# Revit family: 635-00-001 DN100-150
name_source: partatom
category: Pipe Accessories
units: mm (PartAtom-declared; Revit-internal decimal feet)

## family parameters
Always vertical = No
Cut with Voids When Loaded = No
Part Type = Valve - Breaks Into
Round Connector Dimension = Use Diameter
Shared = No
Work Plane-Based = No

## types (3) — shared parameters
1 = 1 mm  [stored 0.00328084 ft]
10 = 10 mm  [stored 0.0328084 ft]
12 = 11 mm  [stored 0.0360892 ft]
2 = 2 mm  [stored 0.00656168 ft]
4 = 4 mm  [stored 0.0131234 ft]
DN100_PN16 = 635-133-00-166
DN125_ PN16 = 635-161-00-166
DN150_ PN16 = 635-188-00-166
Description_ = AVK SUPA MAXI™ TRANSITION COUPLING, PE100/PN16
Search_table = 635-00-001 DN100-150
URL product pages = https://www.avkvalves.com
zero-valued in all types: Default Elevation

## per-type parameters (varying)
- DN100_PN16: Bolt1=9 mm; Bolt2=10.35 mm  [stored 0.0339567 ft]; Bolt_End_dis=74 mm; Bore=50 mm  [stored 0.164042 ft]; Cap_Radius=30 mm  [stored 0.0984252 ft]; D=134 mm; D1=113.9 mm; D2=57.2 mm; D3=40.2 mm  [stored 0.13189 ft]; DN=100 mm; FL_T=61 mm  [stored 0.200131 ft]; FL_T2=30.5 mm  [stored 0.100066 ft]; FLange_T1=81.4 mm; L=547 mm; L1=281 mm; L3=164.1 mm; L4=180.51 mm; L4-L3=11.49 mm; L5=225.64 mm; OD=55 mm  [stored 0.180446 ft]; PCD=120.6 mm; Ring_Dia=72.5 mm  [stored 0.237861 ft]; Ring_Dia1=66.7 mm  [stored 0.218832 ft]; Ring_dia2=60.85 mm; Ring_dia3=66.94 mm; SR1=52 mm; SR2=66.5 mm  [stored 0.218176 ft]; Thickness=11 mm  [stored 0.0360892 ft]
- DN125_ PN16: Bolt1=8.7 mm  [stored 0.0285433 ft]; Bolt2=10.01 mm; Bolt_End_dis=75 mm; Bore=62.5 mm  [stored 0.205052 ft]; Cap_Radius=29 mm  [stored 0.0951444 ft]; D=142.5 mm; D1=121.13 mm; D2=72.6 mm  [stored 0.238189 ft]; D3=42.75 mm  [stored 0.140256 ft]; DN=125 mm; FL_T=56 mm  [stored 0.183727 ft]; FL_T2=28 mm  [stored 0.0918635 ft]; FLange_T1=82.5 mm; L=625 mm; L1=335 mm; L3=187.5 mm; L4=206.25 mm; L4-L3=13.13 mm; L5=257.81 mm; OD=80 mm; PCD=128.25 mm; Ring_Dia=101 mm; Ring_Dia1=92.92 mm; Ring_dia2=86.46 mm; Ring_dia3=95.11 mm; SR1=66 mm  [stored 0.216535 ft]; SR2=79.5 mm; Thickness=16 mm  [stored 0.0524934 ft]
- DN150_ PN16: Bolt1=9.75 mm  [stored 0.0319882 ft]; Bolt2=11.21 mm; Bolt_End_dis=86 mm; Bore=75 mm; Cap_Radius=32.5 mm  [stored 0.106627 ft]; D=117 mm; D1=99.45 mm; D2=87.45 mm; D3=35.1 mm; DN=150 mm; FL_T=67 mm  [stored 0.219816 ft]; FL_T2=33.5 mm; FLange_T1=94.6 mm; L=644 mm; L1=334 mm; L3=193.2 mm; L4=212.52 mm; L4-L3=13.52 mm; L5=265.65 mm; OD=80 mm; PCD=105.3 mm; Ring_Dia=102 mm; Ring_Dia1=93.84 mm; Ring_dia2=86.92 mm; Ring_dia3=95.61 mm; SR1=79.5 mm; SR2=94 mm; Thickness=16 mm  [stored 0.0524934 ft]

note: [stored X ft] marks values corroborated as IEEE doubles in the binary element streams (Revit-internal decimal feet)

## geometry (parser evidence)
native form markers: Sweep x3
no freeform markers — native parametric forms only
